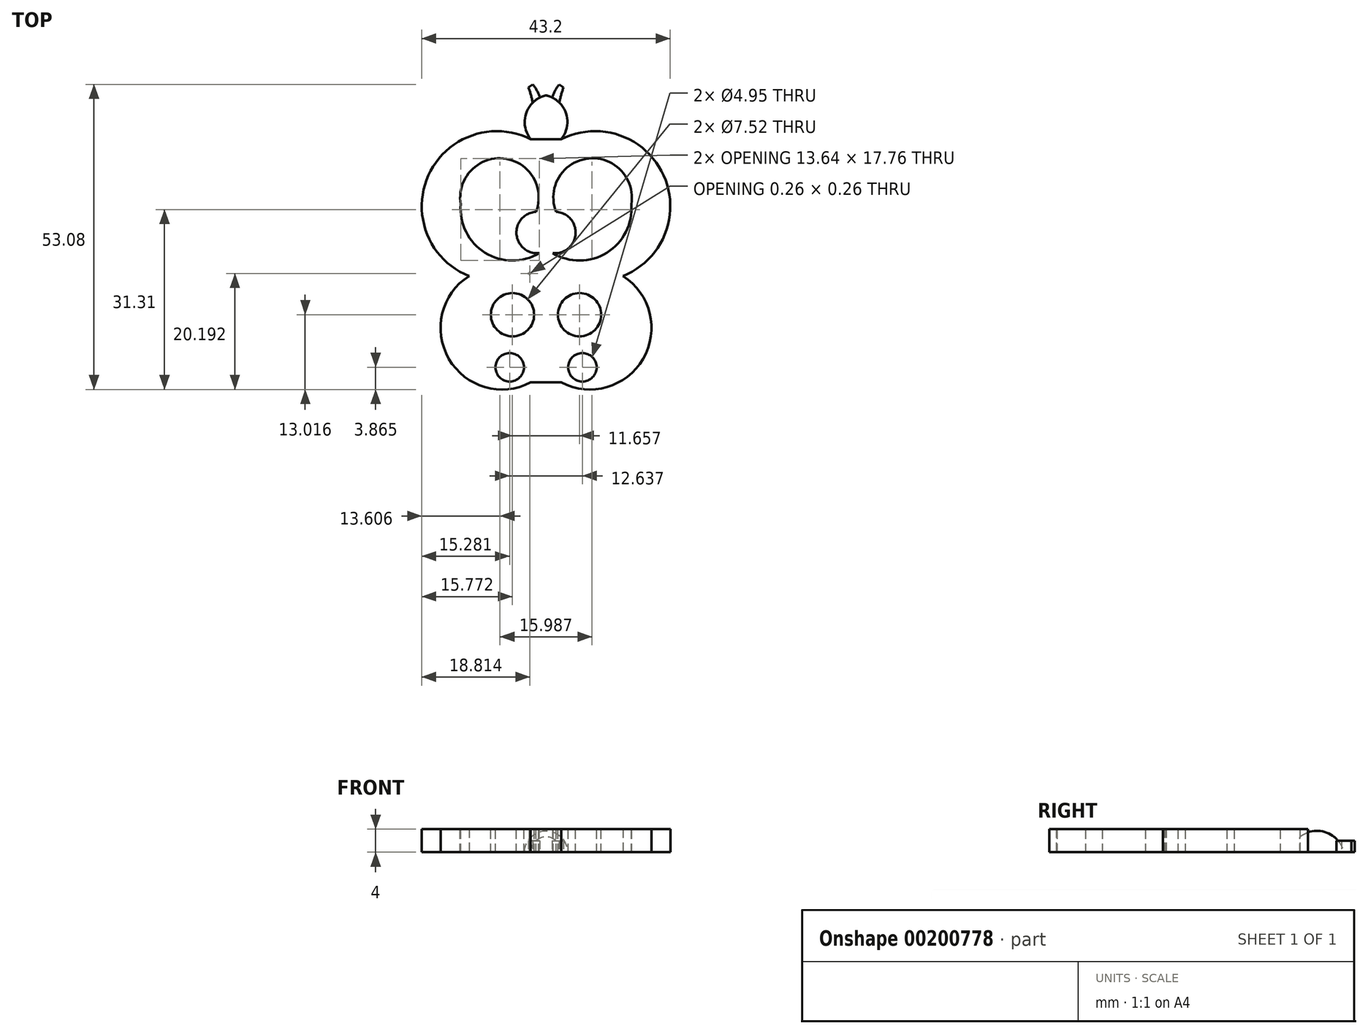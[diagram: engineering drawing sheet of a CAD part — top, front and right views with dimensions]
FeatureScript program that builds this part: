
annotation { "Feature Type Name" : "Feature", "Feature Type Description" : "" }
export const myFeature = defineFeature(function(context is Context, id is Id, definition is map)
    precondition{}
    {
        {
            var Q0;
            Q0=qCreatedBy(makeId("Top.planeOp"),FACE);
            var sketch = newSketch(context, id + "F0", { "sketchPlane" : qUnion([Q0])});
            skLineSegment(sketch, "E0", {"start": v(-2.92, 49) * mm, "end": v(2.66, 49) * mm});
            skLineSegment(sketch, "E1", {"start": v(2.66, 49) * mm, "end": v(2.66, 6.68) * mm});
            skLineSegment(sketch, "E2", {"start": v(-2.92, 49) * mm, "end": v(-2.92, 6.68) * mm});
            skLineSegment(sketch, "E3", {"start": v(-2.92, 6.68) * mm, "end": v(2.66, 6.68) * mm});
            skArc(sketch, "E4", {"start": v(2.66, 25.64) * mm, "mid": v(21.6, 37.32) * mm, "end": v(2.66, 49) * mm});
            skArc(sketch, "E5", {"start": v(2.66, 6.68) * mm, "mid": v(18.33, 16.16) * mm, "end": v(2.66, 25.64) * mm});
            skArc(sketch, "E6.MirrorCS", {"start": v(-2.66, 25.64) * mm, "mid": v(-21.6, 37.32) * mm, "end": v(-2.66, 49) * mm});
            skArc(sketch, "E7.MirrorCS", {"start": v(-2.66, 6.68) * mm, "mid": v(-18.33, 16.16) * mm, "end": v(-2.66, 25.64) * mm});
            skSolve(sketch);
        }
        {
            var Q0;
            {var subQ0=sQuery(id+"F0.wireOp",EDGE,"E2");var subQ1=sQuery(id+"F0.wireOp",EDGE,"E0");var subQ2=makeQuery(id+"F0.imprint","INTERSECT",VERTEX,{"derivedFrom":[subQ1,subQ0]});Q0=makeQuery(id+"F0.imprint","IMPRINT",FACE,{"disambiguationData":[TD([[makeQuery(id+"F0.imprint","IMPRINT",EDGE,{"disambiguationData":[TD([[subQ2,-1.0]])],"derivedFrom":subQ1}),1.0]])]});}
            var Q1;
            {var subQ6=sQuery(id+"F0.wireOp",EDGE,"E0");var subQ12=sQuery(id+"F0.wireOp",EDGE,"E2");var subQ13=makeQuery(id+"F0.imprint","INTERSECT",VERTEX,{"derivedFrom":[subQ6,subQ12]});Q1=makeQuery(id+"F0.imprint","IMPRINT",FACE,{"disambiguationData":[TD([[makeQuery(id+"F0.imprint","IMPRINT",EDGE,{"disambiguationData":[TD([[subQ13,-1.0]])],"derivedFrom":subQ6}),-1.0]])]});}
            var Q2;
            {var subQ0=sQuery(id+"F0.wireOp",EDGE,"E4");var subQ3=sQuery(id+"F0.wireOp",EDGE,"E5");var subQ5=makeQuery(id+"F0.imprint","INTERSECT",VERTEX,{"derivedFrom":[subQ0,subQ3]});Q2=makeQuery(id+"F0.imprint","IMPRINT",FACE,{"disambiguationData":[TD([[makeQuery(id+"F0.imprint","IMPRINT",EDGE,{"disambiguationData":[TD([[subQ5,-1.0]])],"derivedFrom":subQ0}),1.0]])]});}
            var Q3;
            {var subQ0=sQuery(id+"F0.wireOp",EDGE,"E5");var subQ1=sQuery(id+"F0.wireOp",EDGE,"E4");var subQ3=makeQuery(id+"F0.imprint","INTERSECT",VERTEX,{"derivedFrom":[subQ1,subQ0]});Q3=makeQuery(id+"F0.imprint","IMPRINT",FACE,{"disambiguationData":[TD([[makeQuery(id+"F0.imprint","IMPRINT",EDGE,{"disambiguationData":[TD([[subQ3,1.0]])],"derivedFrom":subQ1}),1.0]])]});}
            var Q4;
            {var subQ0=sQuery(id+"F0.wireOp",EDGE,"E5");var subQ3=sQuery(id+"F0.wireOp",EDGE,"E4");var subQ5=makeQuery(id+"F0.imprint","INTERSECT",VERTEX,{"derivedFrom":[subQ3,subQ0]});Q4=makeQuery(id+"F0.imprint","IMPRINT",FACE,{"disambiguationData":[TD([[makeQuery(id+"F0.imprint","IMPRINT",EDGE,{"disambiguationData":[TD([[subQ5,1.0]])],"derivedFrom":subQ3}),-1.0]])]});}
            var Q5;
            {var subQ0=sQuery(id+"F0.wireOp",EDGE,"E3");var subQ1=sQuery(id+"F0.wireOp",EDGE,"E2");var subQ2=makeQuery(id+"F0.imprint","INTERSECT",VERTEX,{"derivedFrom":[subQ1,subQ0]});Q5=makeQuery(id+"F0.imprint","IMPRINT",FACE,{"disambiguationData":[TD([[makeQuery(id+"F0.imprint","IMPRINT",EDGE,{"disambiguationData":[TD([[subQ2,1.0]])],"derivedFrom":subQ1}),-1.0]])]});}
            var Q6;
            {var subQ0=sQuery(id+"F0.wireOp",EDGE,"E7.MirrorCS");var subQ1=sQuery(id+"F0.wireOp",EDGE,"E2");var subQ2=makeQuery(id+"F0.imprint","INTERSECT",VERTEX,{"derivedFrom":[subQ1,subQ0]});Q6=makeQuery(id+"F0.imprint","IMPRINT",FACE,{"disambiguationData":[TD([[makeQuery(id+"F0.imprint","IMPRINT",EDGE,{"disambiguationData":[TD([[subQ2,-1.0]])],"derivedFrom":subQ1}),-1.0]])]});}
            extrude(context, id + "F1", {"entities" : qUnion([Q0, Q1, Q2, Q3, Q4, Q5, Q6]), "depth" : 4 * mm});
        }
        {
            var Q0;
            Q0=qCreatedBy(makeId("Top.planeOp"),FACE);
            var sketch = newSketch(context, id + "F2", { "sketchPlane" : qUnion([Q0])});
            skLineSegment(sketch, "E8", {"start": v(0, 49) * mm, "end": v(0, 56.62) * mm});
            skArc(sketch, "E9", {"start": v(0, 56.62) * mm, "mid": v(-3.45, 53.55) * mm, "end": v(-2.66, 49) * mm});
            skLineSegment(sketch, "E10", {"start": v(-2.66, 49) * mm, "end": v(0, 49) * mm});
            skSolve(sketch);
        }
        {
            var Q0;
            Q0=makeQuery(id+"F2.imprint","IMPRINT",FACE,{"disambiguationData":[TD([[makeQuery(id+"F2.imprint","IMPRINT",EDGE,{"derivedFrom":sQuery(id+"F2.wireOp",EDGE,"E8")}),1.0]])]});
            var Q1;
            Q1=sQuery(id+"F2.wireOp",EDGE,"E8");
            revolve(context, id + "F3", {"operationType" : NewBodyOperationType.ADD, "entities" : qUnion([Q0]), "axis" : qUnion([Q1]), "revolveType" : RevolveType.ONE_DIRECTION, "angle" : 180 * degree});
        }
        {
            var Q0;
            Q0=makeQuery(id+"F3.boolean.opBoolean","MERGE",FACE,{"derivedFrom":[makeQuery(id+"F1.opExtrude","CAP_FACE",FACE,{"disambiguationData":[OSD([sQuery(id+"F0.wireOp",EDGE,"E0"),sQuery(id+"F0.wireOp",EDGE,"E2"),sQuery(id+"F0.wireOp",EDGE,"E3"),sQuery(id+"F0.wireOp",EDGE,"E4"),sQuery(id+"F0.wireOp",EDGE,"E5"),sQuery(id+"F0.wireOp",EDGE,"E6.MirrorCS"),sQuery(id+"F0.wireOp",EDGE,"E7.MirrorCS")])],"isStart":true}),makeQuery(id+"F3.opRevolve","CAP_FACE",FACE,{"disambiguationData":[OSD([sQuery(id+"F2.wireOp",EDGE,"E8"),sQuery(id+"F2.wireOp",EDGE,"E9"),sQuery(id+"F2.wireOp",EDGE,"E10")])],"isStart":true})]});
            var sketch = newSketch(context, id + "F4", { "sketchPlane" : qUnion([Q0])});
            skArc(sketch, "E11", {"start": v(2.66, -49) * mm, "mid": v(0.71, -53.7) * mm, "end": v(2.29, -58.53) * mm});
            skLineSegment(sketch, "E12", {"start": v(2.29, -58.53) * mm, "end": v(3.05, -58) * mm});
            skArc(sketch, "E13", {"start": v(2.66, -49) * mm, "mid": v(2.13, -53.53) * mm, "end": v(3.05, -58) * mm});
            skArc(sketch, "E14.MirrorCS", {"start": v(-2.66, -49) * mm, "mid": v(-0.71, -53.7) * mm, "end": v(-2.29, -58.53) * mm});
            skArc(sketch, "E15.MirrorCS", {"start": v(-2.66, -49) * mm, "mid": v(-2.13, -53.53) * mm, "end": v(-3.05, -58) * mm});
            skLineSegment(sketch, "E16.MirrorCS", {"start": v(-2.29, -58.53) * mm, "end": v(-3.05, -58) * mm});
            skSolve(sketch);
        }
        {
            var Q0;
            {var subQ0=sQuery(id+"F4.wireOp",EDGE,"E12");Q0=makeQuery(id+"F4.imprint","IMPRINT",FACE,{"disambiguationData":[TD([[makeQuery(id+"F4.imprint","IMPRINT",EDGE,{"derivedFrom":subQ0}),1.0]])]});}
            var Q1;
            {var subQ0=sQuery(id+"F4.wireOp",EDGE,"E16.MirrorCS");Q1=makeQuery(id+"F4.imprint","IMPRINT",FACE,{"disambiguationData":[TD([[makeQuery(id+"F4.imprint","IMPRINT",EDGE,{"derivedFrom":subQ0}),-1.0]])]});}
            extrude(context, id + "F5", {"entities" : qUnion([Q0, Q1]), "operationType" : NewBodyOperationType.ADD, "oppositeDirection" : true, "depth" : 2 * mm});
        }
        {
            var Q0;
            Q0=makeQuery(id+"F1.opExtrude","CAP_FACE",FACE,{"disambiguationData":[OSD([sQuery(id+"F0.wireOp",EDGE,"E0"),sQuery(id+"F0.wireOp",EDGE,"E2"),sQuery(id+"F0.wireOp",EDGE,"E3"),sQuery(id+"F0.wireOp",EDGE,"E4"),sQuery(id+"F0.wireOp",EDGE,"E5"),sQuery(id+"F0.wireOp",EDGE,"E6.MirrorCS"),sQuery(id+"F0.wireOp",EDGE,"E7.MirrorCS")])],"isStart":false});
            var sketch = newSketch(context, id + "F6", { "sketchPlane" : qUnion([Q0])});
            skArc(sketch, "E17", {"start": v(-1.74, 36.36) * mm, "mid": v(-5.13, 32.47) * mm, "end": v(-1.17, 29.17) * mm});
            skArc(sketch, "E18", {"start": v(-1.74, 36.36) * mm, "mid": v(-7.42, 45.64) * mm, "end": v(-14.82, 37.67) * mm});
            skArc(sketch, "E19", {"start": v(-14.82, 37.67) * mm, "mid": v(-10.6, 29.24) * mm, "end": v(-1.17, 29.17) * mm});
            skCircle(sketch, "E20", {"center": v(-5.83, 18.47) * mm, "radius": 3.76 * mm});
            skCircle(sketch, "E21", {"center": v(-6.32, 9.31) * mm, "radius": 2.47 * mm});
            skArc(sketch, "E22.MirrorCS", {"start": v(1.74, 36.36) * mm, "mid": v(7.42, 45.64) * mm, "end": v(14.82, 37.67) * mm});
            skArc(sketch, "E23.MirrorCS", {"start": v(14.82, 37.67) * mm, "mid": v(10.6, 29.24) * mm, "end": v(1.17, 29.17) * mm});
            skArc(sketch, "E24.MirrorCS", {"start": v(1.74, 36.36) * mm, "mid": v(5.13, 32.47) * mm, "end": v(1.17, 29.17) * mm});
            skCircle(sketch, "E25.MirrorC", {"center": v(5.83, 18.47) * mm, "radius": 3.76 * mm});
            skCircle(sketch, "E26.MirrorC", {"center": v(6.32, 9.31) * mm, "radius": 2.47 * mm});
            skSolve(sketch);
        }
        {
            var Q0;
            Q0 = qSketchRegion(id + "F6", true);
            extrude(context, id + "F7", {"entities" : qUnion([Q0]), "operationType" : NewBodyOperationType.REMOVE, "endBound" : BoundingType.THROUGH_ALL, "oppositeDirection" : true, "depth" : 25.4 * mm});
        }
    });
